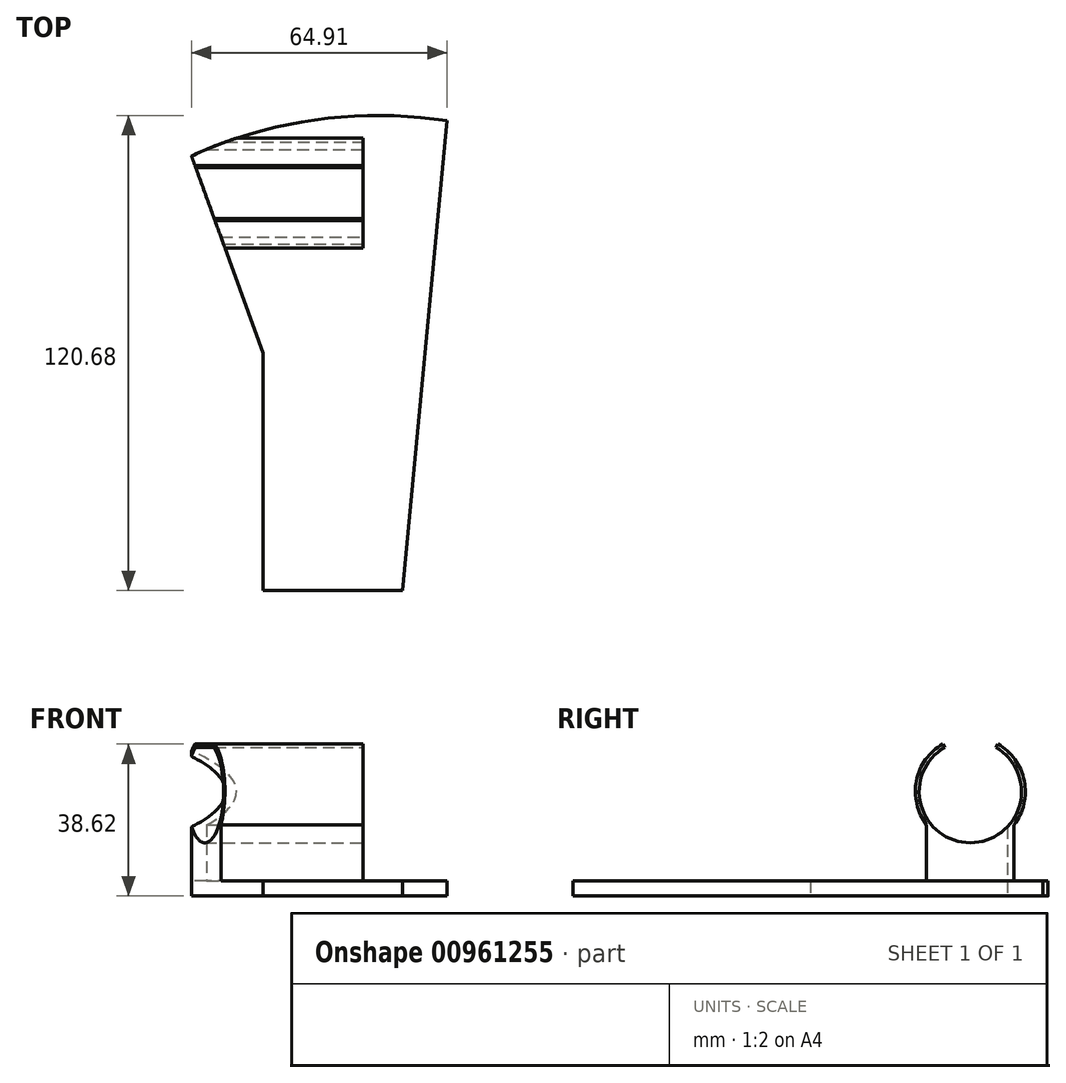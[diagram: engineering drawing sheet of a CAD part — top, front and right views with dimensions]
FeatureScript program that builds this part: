
annotation { "Feature Type Name" : "Feature", "Feature Type Description" : "" }
export const myFeature = defineFeature(function(context is Context, id is Id, definition is map)
    precondition{}
    {
        {
            var Q0;
            Q0=qCreatedBy(makeId("Top.planeOp"),FACE);
            var sketch = newSketch(context, id + "F0", { "sketchPlane" : qUnion([Q0])});
            skLineSegment(sketch, "E0", {"start": v(-32.56, 17.14) * mm, "end": v(32.35, 26.1) * mm});
            skLineSegment(sketch, "E1", {"start": v(32.35, 26.1) * mm, "end": v(21.05, -93.25) * mm});
            skLineSegment(sketch, "E2", {"start": v(21.05, -93.25) * mm, "end": v(-14.33, -93.25) * mm});
            skLineSegment(sketch, "E3", {"start": v(-14.33, -93.25) * mm, "end": v(-14.33, -32.95) * mm});
            skLineSegment(sketch, "E4", {"start": v(-14.33, -32.95) * mm, "end": v(-32.56, 17.14) * mm});
            skArc(sketch, "E5", {"start": v(32.35, 26.1) * mm, "mid": v(-0.76, 26.35) * mm, "end": v(-32.56, 17.14) * mm});
            skSolve(sketch);
        }
        {
            var Q0;
            Q0=makeQuery(id+"F0.imprint","IMPRINT",FACE,{"disambiguationData":[TD([[makeQuery(id+"F0.imprint","IMPRINT",EDGE,{"derivedFrom":sQuery(id+"F0.wireOp",EDGE,"E0")}),1.0]])]});
            var Q1;
            Q1=makeQuery(id+"F0.imprint","IMPRINT",FACE,{"disambiguationData":[TD([[makeQuery(id+"F0.imprint","IMPRINT",EDGE,{"derivedFrom":sQuery(id+"F0.wireOp",EDGE,"E0")}),-1.0]])]});
            extrude(context, id + "F1", {"entities" : qUnion([Q0, Q1]), "depth" : 3.8 * mm, "offsetDistance" : 25.4 * mm});
        }
        {
            var Q0;
            Q0=makeQuery(id+"F1.opExtrude","CAP_FACE",FACE,{"disambiguationData":[OSD([sQuery(id+"F0.wireOp",EDGE,"E1"),sQuery(id+"F0.wireOp",EDGE,"E2"),sQuery(id+"F0.wireOp",EDGE,"E3"),sQuery(id+"F0.wireOp",EDGE,"E4"),sQuery(id+"F0.wireOp",EDGE,"E5")])],"isStart":false});
            var sketch = newSketch(context, id + "F2", { "sketchPlane" : qUnion([Q0])});
            skLineSegment(sketch, "E6.bottom", {"start": v(-43.33, 26.76) * mm, "end": v(11.03, 26.76) * mm});
            skLineSegment(sketch, "E6.top", {"start": v(-43.33, -11.34) * mm, "end": v(11.03, -11.34) * mm});
            skLineSegment(sketch, "E6.left", {"start": v(-43.33, 26.76) * mm, "end": v(-43.33, -11.34) * mm});
            skLineSegment(sketch, "E6.right", {"start": v(11.03, 26.76) * mm, "end": v(11.03, -11.34) * mm});
            skSolve(sketch);
        }
        {
            var Q0;
            Q0=qSketchRegion(id+"F2",true);
            var Q1;
            {var subQ0=sQuery(id+"F2.wireOp",EDGE,"E6.right");Q1=makeQuery(id+"F2.imprint","IMPRINT",FACE,{"disambiguationData":[TD([[makeQuery(id+"F2.imprint","IMPRINT",EDGE,{"derivedFrom":subQ0}),-1.0]])]});}
            extrude(context, id + "F3", {"entities" : qUnion([Q0, Q1]), "operationType" : NewBodyOperationType.ADD, "depth" : 50.8 * mm, "offsetDistance" : 25.4 * mm});
        }
        {
            var Q0;
            Q0=makeQuery(id+"F3.opExtrude","SWEPT_FACE",FACE,{"disambiguationData":[OSD([sQuery(id+"F2.wireOp",EDGE,"E6.right")])]});
            var sketch = newSketch(context, id + "F4", { "sketchPlane" : qUnion([Q0])});
            skLineSegment(sketch, "E7", {"start": v(7.7, 54.61) * mm, "end": v(7.7, 3.81) * mm, "construction": true});
            skArc(sketch, "E8", {"start": v(1.2, 37.78) * mm, "mid": v(7.7, 13.52) * mm, "end": v(14.2, 37.78) * mm});
            skArc(sketch, "E9", {"start": v(18.81, 18.04) * mm, "mid": v(21.4, 29.26) * mm, "end": v(14.7, 38.62) * mm});
            skLineSegment(sketch, "E10", {"start": v(-3.4, 18.04) * mm, "end": v(-3.4, 3.81) * mm});
            skLineSegment(sketch, "E11", {"start": v(-1.4, 15.93) * mm, "end": v(-1.4, 3.81) * mm});
            skLineSegment(sketch, "E12", {"start": v(-1.4, 3.81) * mm, "end": v(-3.4, 3.81) * mm});
            skLineSegment(sketch, "E13.MirrorCS", {"start": v(16.83, 15.93) * mm, "end": v(16.83, 3.81) * mm});
            skLineSegment(sketch, "E14.MirrorCS", {"start": v(18.81, 18.04) * mm, "end": v(18.81, 3.81) * mm});
            skLineSegment(sketch, "E15.MirrorCS", {"start": v(16.83, 3.8) * mm, "end": v(18.81, 3.8) * mm});
            skArc(sketch, "E16.trimOffspring", {"start": v(-1.4, 15.93) * mm, "mid": v(7.7, 12.55) * mm, "end": v(16.83, 15.93) * mm});
            skLineSegment(sketch, "E17", {"start": v(1.2, 37.78) * mm, "end": v(0.72, 38.62) * mm});
            skLineSegment(sketch, "E18.MirrorCS", {"start": v(14.2, 37.78) * mm, "end": v(14.7, 38.62) * mm});
            skArc(sketch, "E19.trimOffspring", {"start": v(0.72, 38.62) * mm, "mid": v(-5.99, 29.26) * mm, "end": v(-3.4, 18.04) * mm});
            skSolve(sketch);
        }
        {
            var Q0;
            Q0=makeQuery(id+"F4.imprint","IMPRINT",FACE,{"disambiguationData":[TD([[makeQuery(id+"F4.imprint","IMPRINT",EDGE,{"derivedFrom":sQuery(id+"F4.wireOp",EDGE,"E9")}),-1.0]])]});
            var Q1;
            Q1=makeQuery(id+"F4.imprint","IMPRINT",FACE,{"disambiguationData":[TD([[makeQuery(id+"F4.imprint","IMPRINT",EDGE,{"derivedFrom":sQuery(id+"F4.wireOp",EDGE,"E8")}),1.0]])]});
            extrude(context, id + "F5", {"entities" : qUnion([Q0, Q1]), "operationType" : NewBodyOperationType.REMOVE, "endBound" : BoundingType.THROUGH_ALL, "oppositeDirection" : true, "depth" : 25.4 * mm, "offsetDistance" : 25.4 * mm});
        }
        {
            var Q0;
            Q0=makeQuery(id+"F1.opExtrude","CAP_FACE",FACE,{"disambiguationData":[OSD([sQuery(id+"F0.wireOp",EDGE,"E1"),sQuery(id+"F0.wireOp",EDGE,"E2"),sQuery(id+"F0.wireOp",EDGE,"E3"),sQuery(id+"F0.wireOp",EDGE,"E4"),sQuery(id+"F0.wireOp",EDGE,"E5")])],"isStart":true});
            var sketch = newSketch(context, id + "F6", { "sketchPlane" : qUnion([Q0])});
            skArc(sketch, "E20", {"start": v(-32.56, -17.14) * mm, "mid": v(-22.05, -21.36) * mm, "end": v(-11.14, -24.43) * mm});
            skLineSegment(sketch, "E21", {"start": v(-32.56, -17.14) * mm, "end": v(-22.96, 9.24) * mm});
            skLineSegment(sketch, "E22", {"start": v(-22.96, 9.24) * mm, "end": v(-11.14, -24.43) * mm});
            skLineSegment(sketch, "E23", {"start": v(-11.14, -24.43) * mm, "end": v(-60.05, -34.57) * mm});
            skLineSegment(sketch, "E24", {"start": v(-60.05, -34.57) * mm, "end": v(-52.27, 17.83) * mm});
            skLineSegment(sketch, "E25", {"start": v(-52.27, 17.83) * mm, "end": v(-22.96, 9.24) * mm});
            skSolve(sketch);
        }
        {
            var Q0;
            Q0=makeQuery(id+"F6.imprint","IMPRINT",FACE,{"disambiguationData":[TD([[makeQuery(id+"F6.imprint","IMPRINT",EDGE,{"derivedFrom":sQuery(id+"F6.wireOp",EDGE,"E20")}),-1.0]])]});
            extrude(context, id + "F7", {"entities" : qUnion([Q0]), "operationType" : NewBodyOperationType.REMOVE, "endBound" : BoundingType.THROUGH_ALL, "oppositeDirection" : true, "depth" : 25.4 * mm, "offsetDistance" : 25.4 * mm});
        }
    });
